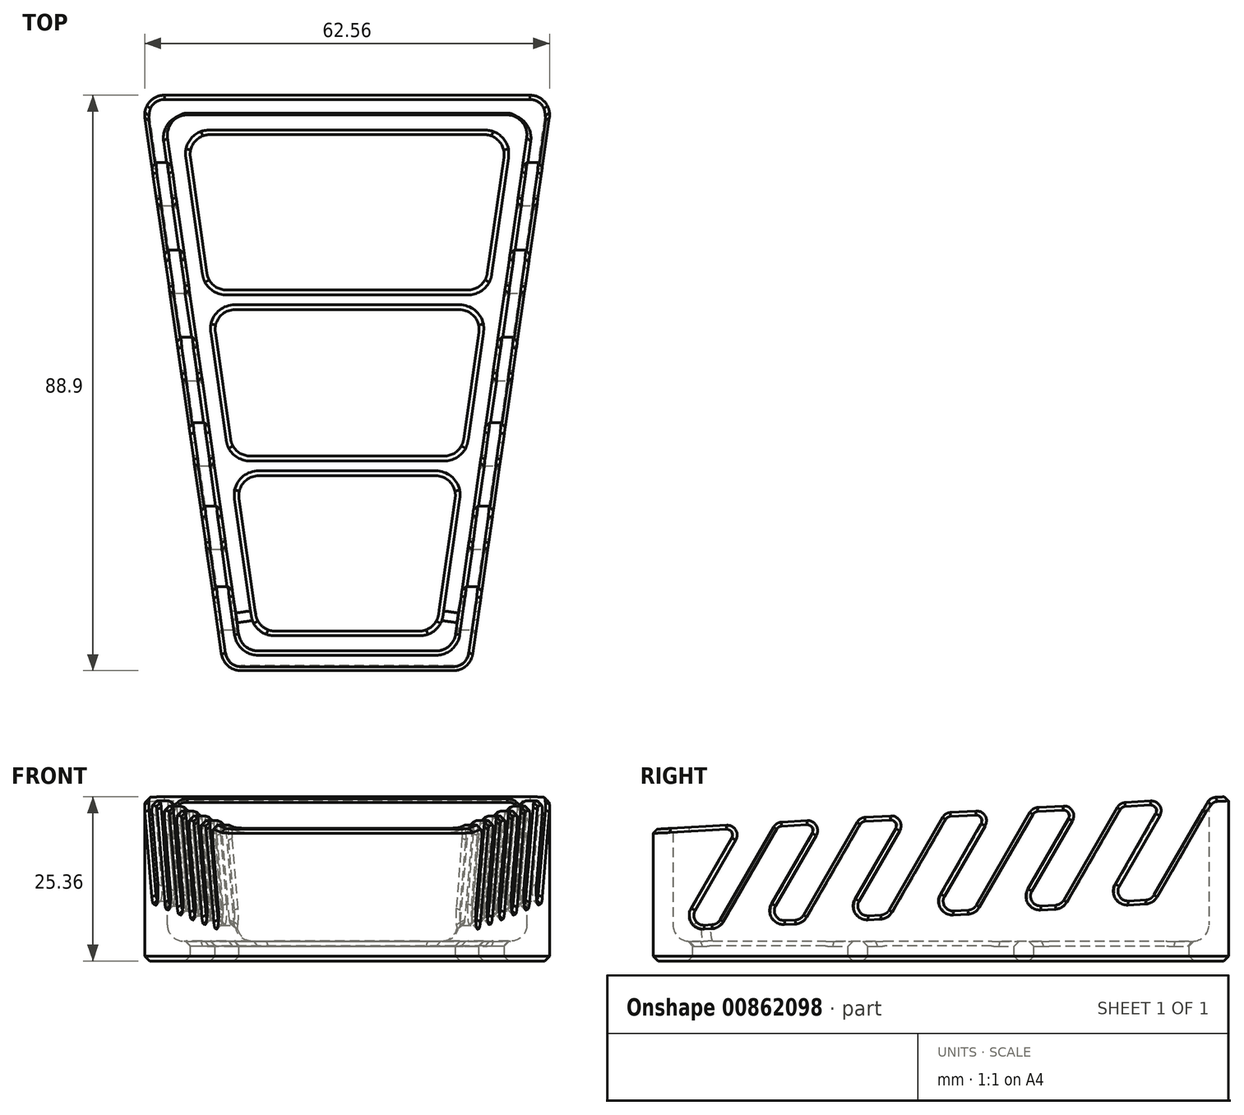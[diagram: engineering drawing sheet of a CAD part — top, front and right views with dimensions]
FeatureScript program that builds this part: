
annotation { "Feature Type Name" : "Feature", "Feature Type Description" : "" }
export const myFeature = defineFeature(function(context is Context, id is Id, definition is map)
    precondition{}
    {
        {
            var Q0;
            Q0=qCreatedBy(makeId("Top.planeOp"),FACE);
            var sketch = newSketch(context, id + "F0", { "sketchPlane" : qUnion([Q0])});
            skLineSegment(sketch, "E0", {"start": v(-122.84, 0) * mm, "end": v(0, 0) * mm, "construction": true});
            skLineSegment(sketch, "E1", {"start": v(0, 0) * mm, "end": v(0, 214.45) * mm, "construction": true});
            skLineSegment(sketch, "E2", {"start": v(-19.05, 0) * mm, "end": v(-31.75, 88.9) * mm});
            skLineSegment(sketch, "E3", {"start": v(-31.75, 88.9) * mm, "end": v(31.75, 88.9) * mm});
            skLineSegment(sketch, "E4", {"start": v(31.75, 88.9) * mm, "end": v(19.05, 0) * mm});
            skLineSegment(sketch, "E5", {"start": v(19.05, 0) * mm, "end": v(-19.05, 0) * mm});
            skSolve(sketch);
        }
        {
            var Q0;
            Q0 = qSketchRegion(id + "F0", true);
            extrude(context, id + "F1", {"entities" : qUnion([Q0]), "depth" : 25.4 * mm, "offsetDistance" : 25.4 * mm});
        }
        {
            var Q0;
            Q0=makeQuery(id+"F1.opExtrude","CAP_FACE",FACE,{"disambiguationData":[OSD([sQuery(id+"F0.wireOp",EDGE,"E2"),sQuery(id+"F0.wireOp",EDGE,"E3"),sQuery(id+"F0.wireOp",EDGE,"E4"),sQuery(id+"F0.wireOp",EDGE,"E5")])],"isStart":false});
            shell(context, id + "F2", {"entities" : qUnion([Q0]), "thickness" : 3.05 * mm});
        }
        {
            var Q0;
            Q0=qCreatedBy(makeId("Right.planeOp"),FACE);
            var sketch = newSketch(context, id + "F3", { "sketchPlane" : qUnion([Q0])});
            skLineSegment(sketch, "E6", {"start": v(88.9, 38.83) * mm, "end": v(88.9, 0) * mm, "construction": true});
            skLineSegment(sketch, "E7", {"start": v(0, 38.83) * mm, "end": v(0, 0) * mm, "construction": true});
            skLineSegment(sketch, "E8", {"start": v(0, 5.08) * mm, "end": v(88.9, 10.16) * mm, "construction": true});
            skLineSegment(sketch, "E9", {"start": v(101.6, 38.83) * mm, "end": v(-12.7, 38.83) * mm});
            skLineSegment(sketch, "E10", {"start": v(-12.7, 38.83) * mm, "end": v(-12.7, 19.6) * mm});
            skLineSegment(sketch, "E11", {"start": v(101.6, 38.83) * mm, "end": v(101.6, 26.13) * mm});
            skLineSegment(sketch, "E12", {"start": v(-12.7, 19.6) * mm, "end": v(14.18, 21.13) * mm});
            skLineSegment(sketch, "E13", {"start": v(16.6, 21.27) * mm, "end": v(7.5, 5.5) * mm, "construction": true});
            skLineSegment(sketch, "E14", {"start": v(29.27, 22) * mm, "end": v(20.17, 6.23) * mm, "construction": true});
            skLineSegment(sketch, "E15", {"start": v(42.31, 22.74) * mm, "end": v(33.21, 6.98) * mm, "construction": true});
            skLineSegment(sketch, "E16", {"start": v(55.66, 23.5) * mm, "end": v(46.56, 7.74) * mm, "construction": true});
            skLineSegment(sketch, "E17", {"start": v(69.15, 24.27) * mm, "end": v(60.05, 8.51) * mm, "construction": true});
            skLineSegment(sketch, "E18", {"start": v(82.88, 25.06) * mm, "end": v(73.78, 9.3) * mm, "construction": true});
            skLineSegment(sketch, "E19", {"start": v(14.18, 21.13) * mm, "end": v(5.08, 5.37) * mm});
            skLineSegment(sketch, "E20", {"start": v(5.08, 5.37) * mm, "end": v(9.93, 5.65) * mm});
            skLineSegment(sketch, "E21", {"start": v(9.93, 5.65) * mm, "end": v(19.03, 21.4) * mm});
            skLineSegment(sketch, "E22", {"start": v(26.61, 21.84) * mm, "end": v(17.52, 6.08) * mm});
            skLineSegment(sketch, "E23", {"start": v(17.52, 6.08) * mm, "end": v(22.82, 6.38) * mm});
            skLineSegment(sketch, "E24", {"start": v(22.82, 6.38) * mm, "end": v(31.92, 22.14) * mm});
            skLineSegment(sketch, "E25", {"start": v(39.5, 22.58) * mm, "end": v(30.4, 6.82) * mm});
            skLineSegment(sketch, "E26", {"start": v(30.4, 6.82) * mm, "end": v(36.02, 7.14) * mm});
            skLineSegment(sketch, "E27", {"start": v(36.02, 7.14) * mm, "end": v(45.12, 22.9) * mm});
            skLineSegment(sketch, "E28", {"start": v(52.7, 23.33) * mm, "end": v(43.6, 7.57) * mm});
            skLineSegment(sketch, "E29", {"start": v(43.6, 7.57) * mm, "end": v(49.51, 7.9) * mm});
            skLineSegment(sketch, "E30", {"start": v(49.51, 7.9) * mm, "end": v(58.61, 23.67) * mm});
            skLineSegment(sketch, "E31", {"start": v(66.2, 24.1) * mm, "end": v(57.1, 8.34) * mm});
            skLineSegment(sketch, "E32", {"start": v(57.1, 8.34) * mm, "end": v(63.01, 8.68) * mm});
            skLineSegment(sketch, "E33", {"start": v(63.01, 8.68) * mm, "end": v(72.1, 24.44) * mm});
            skLineSegment(sketch, "E34", {"start": v(79.7, 24.87) * mm, "end": v(70.6, 9.11) * mm});
            skLineSegment(sketch, "E35", {"start": v(70.6, 9.11) * mm, "end": v(76.96, 9.48) * mm});
            skLineSegment(sketch, "E36", {"start": v(76.96, 9.48) * mm, "end": v(86.06, 25.24) * mm});
            skPoint(sketch, "E37", {"position": v(0, 20.32) * mm});
            skPoint(sketch, "E38", {"position": v(88.9, 25.4) * mm});
            skLineSegment(sketch, "E39.trimOffspring", {"start": v(19.03, 21.4) * mm, "end": v(26.61, 21.84) * mm});
            skLineSegment(sketch, "E40.trimOffspring", {"start": v(31.92, 22.14) * mm, "end": v(39.5, 22.58) * mm});
            skLineSegment(sketch, "E41.trimOffspring", {"start": v(45.12, 22.9) * mm, "end": v(52.7, 23.33) * mm});
            skLineSegment(sketch, "E42.trimOffspring", {"start": v(58.61, 23.67) * mm, "end": v(66.2, 24.1) * mm});
            skLineSegment(sketch, "E43.trimOffspring", {"start": v(72.1, 24.44) * mm, "end": v(79.7, 24.87) * mm});
            skLineSegment(sketch, "E44.trimOffspring", {"start": v(86.06, 25.24) * mm, "end": v(101.6, 26.13) * mm});
            skSolve(sketch);
        }
        {
            var Q0;
            Q0=makeQuery(id+"F3.imprint","IMPRINT",FACE,{"disambiguationData":[TD([[makeQuery(id+"F3.imprint","IMPRINT",EDGE,{"derivedFrom":sQuery(id+"F3.wireOp",EDGE,"E9")}),1.0]])]});
            extrude(context, id + "F4", {"entities" : qUnion([Q0]), "operationType" : NewBodyOperationType.REMOVE, "endBound" : BoundingType.THROUGH_ALL, "depth" : 25.4 * mm, "offsetDistance" : 25.4 * mm, "hasSecondDirection" : true, "secondDirectionBound" : SecondDirectionBoundingType.THROUGH_ALL, "secondDirectionOppositeDirection" : true, "secondDirectionDepth" : 25.4 * mm});
        }
        {
            var Q0;
            Q0=makeQuery(id+"F2.opShell","OFFSET_FACE",FACE,{"disambiguationData":[OSD([sQuery(id+"F0.wireOp",EDGE,"E2"),sQuery(id+"F0.wireOp",EDGE,"E3"),sQuery(id+"F0.wireOp",EDGE,"E4"),sQuery(id+"F0.wireOp",EDGE,"E5")])]});
            var sketch = newSketch(context, id + "F5", { "sketchPlane" : qUnion([Q0])});
            skLineSegment(sketch, "E45", {"start": v(-38.97, 0) * mm, "end": v(0, 0) * mm, "construction": true});
            skLineSegment(sketch, "E46", {"start": v(0, 0) * mm, "end": v(0, 92.83) * mm, "construction": true});
            skLineSegment(sketch, "E47", {"start": v(-13.76, 6.1) * mm, "end": v(13.76, 6.1) * mm});
            skLineSegment(sketch, "E48", {"start": v(13.76, 6.1) * mm, "end": v(17.2, 30.1) * mm});
            skLineSegment(sketch, "E49", {"start": v(24.72, 82.8) * mm, "end": v(-24.72, 82.8) * mm});
            skLineSegment(sketch, "E50", {"start": v(-24.72, 82.8) * mm, "end": v(-21.3, 58.8) * mm});
            skLineSegment(sketch, "E51", {"start": v(-36.35, 31.62) * mm, "end": v(27.15, 31.62) * mm, "construction": true});
            skLineSegment(sketch, "E52", {"start": v(-39.3, 57.28) * mm, "end": v(34.58, 57.28) * mm, "construction": true});
            skLineSegment(sketch, "E53", {"start": v(-17.2, 30.1) * mm, "end": v(17.2, 30.1) * mm});
            skLineSegment(sketch, "E54", {"start": v(-17.63, 33.15) * mm, "end": v(17.63, 33.15) * mm});
            skLineSegment(sketch, "E55", {"start": v(-20.86, 55.75) * mm, "end": v(20.86, 55.75) * mm});
            skLineSegment(sketch, "E56", {"start": v(-21.3, 58.8) * mm, "end": v(21.3, 58.8) * mm});
            skLineSegment(sketch, "E57.trimOffspring", {"start": v(-17.2, 30.1) * mm, "end": v(-13.76, 6.1) * mm});
            skLineSegment(sketch, "E58.trimOffspring", {"start": v(-20.86, 55.75) * mm, "end": v(-17.63, 33.15) * mm});
            skLineSegment(sketch, "E59.trimOffspring", {"start": v(21.3, 58.8) * mm, "end": v(24.72, 82.8) * mm});
            skLineSegment(sketch, "E60.trimOffspring", {"start": v(17.63, 33.15) * mm, "end": v(20.86, 55.75) * mm});
            skSolve(sketch);
        }
        {
            var Q0;
            Q0=makeQuery(id+"F5.imprint","IMPRINT",FACE,{"disambiguationData":[TD([[makeQuery(id+"F5.imprint","IMPRINT",EDGE,{"derivedFrom":sQuery(id+"F5.wireOp",EDGE,"E47")}),1.0]])]});
            var Q1;
            Q1=makeQuery(id+"F5.imprint","IMPRINT",FACE,{"disambiguationData":[TD([[makeQuery(id+"F5.imprint","IMPRINT",EDGE,{"derivedFrom":sQuery(id+"F5.wireOp",EDGE,"E54")}),1.0]])]});
            var Q2;
            Q2=makeQuery(id+"F5.imprint","IMPRINT",FACE,{"disambiguationData":[TD([[makeQuery(id+"F5.imprint","IMPRINT",EDGE,{"derivedFrom":sQuery(id+"F5.wireOp",EDGE,"E49")}),1.0]])]});
            extrude(context, id + "F6", {"entities" : qUnion([Q0, Q1, Q2]), "operationType" : NewBodyOperationType.REMOVE, "oppositeDirection" : true, "depth" : 25.4 * mm, "offsetDistance" : 25.4 * mm});
        }
        {
            var Q0;
            Q0=makeQuery(id+"F6.boolean.opBoolean","COPY",EDGE,{"derivedFrom":makeQuery(id+"F6.opExtrude","SWEPT_EDGE",EDGE,{"disambiguationData":[OSD([sQuery(id+"F5.wireOp",EDGE,"E53"),sQuery(id+"F5.wireOp",EDGE,"E57.trimOffspring")])]})});
            var Q1;
            Q1=makeQuery(id+"F6.boolean.opBoolean","COPY",EDGE,{"derivedFrom":makeQuery(id+"F6.opExtrude","SWEPT_EDGE",EDGE,{"disambiguationData":[OSD([sQuery(id+"F5.wireOp",EDGE,"E54"),sQuery(id+"F5.wireOp",EDGE,"E58.trimOffspring")])]})});
            var Q2;
            Q2=makeQuery(id+"F6.boolean.opBoolean","COPY",EDGE,{"derivedFrom":makeQuery(id+"F6.opExtrude","SWEPT_EDGE",EDGE,{"disambiguationData":[OSD([sQuery(id+"F5.wireOp",EDGE,"E55"),sQuery(id+"F5.wireOp",EDGE,"E58.trimOffspring")])]})});
            var Q3;
            Q3=makeQuery(id+"F6.boolean.opBoolean","COPY",EDGE,{"derivedFrom":makeQuery(id+"F6.opExtrude","SWEPT_EDGE",EDGE,{"disambiguationData":[OSD([sQuery(id+"F5.wireOp",EDGE,"E50"),sQuery(id+"F5.wireOp",EDGE,"E56")])]})});
            var Q4;
            Q4=makeQuery(id+"F6.boolean.opBoolean","COPY",EDGE,{"derivedFrom":makeQuery(id+"F6.opExtrude","SWEPT_EDGE",EDGE,{"disambiguationData":[OSD([sQuery(id+"F5.wireOp",EDGE,"E47"),sQuery(id+"F5.wireOp",EDGE,"E57.trimOffspring")])]})});
            var Q5;
            Q5=makeQuery(id+"F6.boolean.opBoolean","COPY",EDGE,{"derivedFrom":makeQuery(id+"F6.opExtrude","SWEPT_EDGE",EDGE,{"disambiguationData":[OSD([sQuery(id+"F5.wireOp",EDGE,"E49"),sQuery(id+"F5.wireOp",EDGE,"E50")])]})});
            var Q6;
            Q6=makeQuery(id+"F6.boolean.opBoolean","COPY",EDGE,{"derivedFrom":makeQuery(id+"F6.opExtrude","SWEPT_EDGE",EDGE,{"disambiguationData":[OSD([sQuery(id+"F5.wireOp",EDGE,"E49"),sQuery(id+"F5.wireOp",EDGE,"E59.trimOffspring")])]})});
            var Q7;
            Q7=makeQuery(id+"F6.boolean.opBoolean","COPY",EDGE,{"derivedFrom":makeQuery(id+"F6.opExtrude","SWEPT_EDGE",EDGE,{"disambiguationData":[OSD([sQuery(id+"F5.wireOp",EDGE,"E55"),sQuery(id+"F5.wireOp",EDGE,"E60.trimOffspring")])]})});
            var Q8;
            Q8=makeQuery(id+"F6.boolean.opBoolean","COPY",EDGE,{"derivedFrom":makeQuery(id+"F6.opExtrude","SWEPT_EDGE",EDGE,{"disambiguationData":[OSD([sQuery(id+"F5.wireOp",EDGE,"E48"),sQuery(id+"F5.wireOp",EDGE,"E53")])]})});
            var Q9;
            Q9=makeQuery(id+"F6.boolean.opBoolean","COPY",EDGE,{"derivedFrom":makeQuery(id+"F6.opExtrude","SWEPT_EDGE",EDGE,{"disambiguationData":[OSD([sQuery(id+"F5.wireOp",EDGE,"E47"),sQuery(id+"F5.wireOp",EDGE,"E48")])]})});
            var Q10;
            Q10=makeQuery(id+"F6.boolean.opBoolean","COPY",EDGE,{"derivedFrom":makeQuery(id+"F6.opExtrude","SWEPT_EDGE",EDGE,{"disambiguationData":[OSD([sQuery(id+"F5.wireOp",EDGE,"E54"),sQuery(id+"F5.wireOp",EDGE,"E60.trimOffspring")])]})});
            var Q11;
            Q11=makeQuery(id+"F6.boolean.opBoolean","COPY",EDGE,{"derivedFrom":makeQuery(id+"F6.opExtrude","SWEPT_EDGE",EDGE,{"disambiguationData":[OSD([sQuery(id+"F5.wireOp",EDGE,"E56"),sQuery(id+"F5.wireOp",EDGE,"E59.trimOffspring")])]})});
            fillet(context, id + "F7", {"entities" : qUnion([Q0, Q1, Q2, Q3, Q4, Q5, Q6, Q7, Q8, Q9, Q10, Q11]), "radius" : 3.05 * mm, "tangentPropagation" : true, "allowEdgeOverflow" : false});
        }
        {
            var Q0;
            {var subQ0=sQuery(id+"F0.wireOp",EDGE,"E4");var subQ1=sQuery(id+"F3.wireOp",EDGE,"E19");var subQ2=sQuery(id+"F3.wireOp",EDGE,"E20");Q0=makeQuery(id+"F4.boolean.opBoolean","COPY",EDGE,{"disambiguationData":[TD([makeQuery(id+"F1.opExtrude","SWEPT_FACE",FACE,{"disambiguationData":[OSD([subQ0])]})])],"derivedFrom":makeQuery(id+"F4.opExtrude","SWEPT_EDGE",EDGE,{"disambiguationData":[OSD([subQ1,subQ2])]})});}
            var Q1;
            {var subQ0=sQuery(id+"F0.wireOp",EDGE,"E4");var subQ1=sQuery(id+"F3.wireOp",EDGE,"E20");var subQ2=sQuery(id+"F3.wireOp",EDGE,"E21");Q1=makeQuery(id+"F4.boolean.opBoolean","COPY",EDGE,{"disambiguationData":[TD([makeQuery(id+"F1.opExtrude","SWEPT_FACE",FACE,{"disambiguationData":[OSD([subQ0])]})])],"derivedFrom":makeQuery(id+"F4.opExtrude","SWEPT_EDGE",EDGE,{"disambiguationData":[OSD([subQ1,subQ2])]})});}
            var Q2;
            {var subQ0=sQuery(id+"F0.wireOp",EDGE,"E4");var subQ1=sQuery(id+"F3.wireOp",EDGE,"E12");var subQ2=sQuery(id+"F3.wireOp",EDGE,"E19");Q2=makeQuery(id+"F4.boolean.opBoolean","COPY",EDGE,{"disambiguationData":[TD([makeQuery(id+"F1.opExtrude","SWEPT_FACE",FACE,{"disambiguationData":[OSD([subQ0])]})])],"derivedFrom":makeQuery(id+"F4.opExtrude","SWEPT_EDGE",EDGE,{"disambiguationData":[OSD([subQ1,subQ2])]})});}
            var Q3;
            {var subQ0=sQuery(id+"F0.wireOp",EDGE,"E4");var subQ1=sQuery(id+"F3.wireOp",EDGE,"E21");var subQ2=sQuery(id+"F3.wireOp",EDGE,"E39.trimOffspring");Q3=makeQuery(id+"F4.boolean.opBoolean","COPY",EDGE,{"disambiguationData":[TD([makeQuery(id+"F1.opExtrude","SWEPT_FACE",FACE,{"disambiguationData":[OSD([subQ0])]})])],"derivedFrom":makeQuery(id+"F4.opExtrude","SWEPT_EDGE",EDGE,{"disambiguationData":[OSD([subQ1,subQ2])]})});}
            var Q4;
            {var subQ0=sQuery(id+"F0.wireOp",EDGE,"E4");var subQ1=sQuery(id+"F3.wireOp",EDGE,"E22");var subQ2=sQuery(id+"F3.wireOp",EDGE,"E39.trimOffspring");Q4=makeQuery(id+"F4.boolean.opBoolean","COPY",EDGE,{"disambiguationData":[TD([makeQuery(id+"F1.opExtrude","SWEPT_FACE",FACE,{"disambiguationData":[OSD([subQ0])]})])],"derivedFrom":makeQuery(id+"F4.opExtrude","SWEPT_EDGE",EDGE,{"disambiguationData":[OSD([subQ1,subQ2])]})});}
            var Q5;
            {var subQ0=sQuery(id+"F0.wireOp",EDGE,"E4");var subQ1=sQuery(id+"F3.wireOp",EDGE,"E40.trimOffspring");var subQ2=sQuery(id+"F3.wireOp",EDGE,"E24");Q5=makeQuery(id+"F4.boolean.opBoolean","COPY",EDGE,{"disambiguationData":[TD([makeQuery(id+"F1.opExtrude","SWEPT_FACE",FACE,{"disambiguationData":[OSD([subQ0])]})])],"derivedFrom":makeQuery(id+"F4.opExtrude","SWEPT_EDGE",EDGE,{"disambiguationData":[OSD([subQ2,subQ1])]})});}
            var Q6;
            {var subQ0=sQuery(id+"F0.wireOp",EDGE,"E4");var subQ1=sQuery(id+"F3.wireOp",EDGE,"E23");var subQ2=sQuery(id+"F3.wireOp",EDGE,"E22");Q6=makeQuery(id+"F4.boolean.opBoolean","COPY",EDGE,{"disambiguationData":[TD([makeQuery(id+"F1.opExtrude","SWEPT_FACE",FACE,{"disambiguationData":[OSD([subQ0])]})])],"derivedFrom":makeQuery(id+"F4.opExtrude","SWEPT_EDGE",EDGE,{"disambiguationData":[OSD([subQ2,subQ1])]})});}
            var Q7;
            {var subQ0=sQuery(id+"F0.wireOp",EDGE,"E4");var subQ1=sQuery(id+"F3.wireOp",EDGE,"E23");var subQ2=sQuery(id+"F3.wireOp",EDGE,"E24");Q7=makeQuery(id+"F4.boolean.opBoolean","COPY",EDGE,{"disambiguationData":[TD([makeQuery(id+"F1.opExtrude","SWEPT_FACE",FACE,{"disambiguationData":[OSD([subQ0])]})])],"derivedFrom":makeQuery(id+"F4.opExtrude","SWEPT_EDGE",EDGE,{"disambiguationData":[OSD([subQ1,subQ2])]})});}
            var Q8;
            {var subQ0=sQuery(id+"F0.wireOp",EDGE,"E4");var subQ1=sQuery(id+"F3.wireOp",EDGE,"E40.trimOffspring");var subQ2=sQuery(id+"F3.wireOp",EDGE,"E25");Q8=makeQuery(id+"F4.boolean.opBoolean","COPY",EDGE,{"disambiguationData":[TD([makeQuery(id+"F1.opExtrude","SWEPT_FACE",FACE,{"disambiguationData":[OSD([subQ0])]})])],"derivedFrom":makeQuery(id+"F4.opExtrude","SWEPT_EDGE",EDGE,{"disambiguationData":[OSD([subQ2,subQ1])]})});}
            var Q9;
            {var subQ0=sQuery(id+"F0.wireOp",EDGE,"E4");var subQ1=sQuery(id+"F3.wireOp",EDGE,"E27");var subQ2=sQuery(id+"F3.wireOp",EDGE,"E41.trimOffspring");Q9=makeQuery(id+"F4.boolean.opBoolean","COPY",EDGE,{"disambiguationData":[TD([makeQuery(id+"F1.opExtrude","SWEPT_FACE",FACE,{"disambiguationData":[OSD([subQ0])]})])],"derivedFrom":makeQuery(id+"F4.opExtrude","SWEPT_EDGE",EDGE,{"disambiguationData":[OSD([subQ1,subQ2])]})});}
            var Q10;
            {var subQ0=sQuery(id+"F0.wireOp",EDGE,"E4");var subQ1=sQuery(id+"F3.wireOp",EDGE,"E26");var subQ2=sQuery(id+"F3.wireOp",EDGE,"E27");Q10=makeQuery(id+"F4.boolean.opBoolean","COPY",EDGE,{"disambiguationData":[TD([makeQuery(id+"F1.opExtrude","SWEPT_FACE",FACE,{"disambiguationData":[OSD([subQ0])]})])],"derivedFrom":makeQuery(id+"F4.opExtrude","SWEPT_EDGE",EDGE,{"disambiguationData":[OSD([subQ1,subQ2])]})});}
            var Q11;
            {var subQ0=sQuery(id+"F0.wireOp",EDGE,"E4");var subQ1=sQuery(id+"F3.wireOp",EDGE,"E25");var subQ2=sQuery(id+"F3.wireOp",EDGE,"E26");Q11=makeQuery(id+"F4.boolean.opBoolean","COPY",EDGE,{"disambiguationData":[TD([makeQuery(id+"F1.opExtrude","SWEPT_FACE",FACE,{"disambiguationData":[OSD([subQ0])]})])],"derivedFrom":makeQuery(id+"F4.opExtrude","SWEPT_EDGE",EDGE,{"disambiguationData":[OSD([subQ1,subQ2])]})});}
            var Q12;
            {var subQ0=sQuery(id+"F0.wireOp",EDGE,"E4");var subQ1=sQuery(id+"F3.wireOp",EDGE,"E28");var subQ2=sQuery(id+"F3.wireOp",EDGE,"E29");Q12=makeQuery(id+"F4.boolean.opBoolean","COPY",EDGE,{"disambiguationData":[TD([makeQuery(id+"F1.opExtrude","SWEPT_FACE",FACE,{"disambiguationData":[OSD([subQ0])]})])],"derivedFrom":makeQuery(id+"F4.opExtrude","SWEPT_EDGE",EDGE,{"disambiguationData":[OSD([subQ1,subQ2])]})});}
            var Q13;
            {var subQ0=sQuery(id+"F0.wireOp",EDGE,"E4");var subQ1=sQuery(id+"F3.wireOp",EDGE,"E28");var subQ2=sQuery(id+"F3.wireOp",EDGE,"E41.trimOffspring");Q13=makeQuery(id+"F4.boolean.opBoolean","COPY",EDGE,{"disambiguationData":[TD([makeQuery(id+"F1.opExtrude","SWEPT_FACE",FACE,{"disambiguationData":[OSD([subQ0])]})])],"derivedFrom":makeQuery(id+"F4.opExtrude","SWEPT_EDGE",EDGE,{"disambiguationData":[OSD([subQ1,subQ2])]})});}
            var Q14;
            {var subQ0=sQuery(id+"F0.wireOp",EDGE,"E4");var subQ1=sQuery(id+"F3.wireOp",EDGE,"E30");var subQ2=sQuery(id+"F3.wireOp",EDGE,"E42.trimOffspring");Q14=makeQuery(id+"F4.boolean.opBoolean","COPY",EDGE,{"disambiguationData":[TD([makeQuery(id+"F1.opExtrude","SWEPT_FACE",FACE,{"disambiguationData":[OSD([subQ0])]})])],"derivedFrom":makeQuery(id+"F4.opExtrude","SWEPT_EDGE",EDGE,{"disambiguationData":[OSD([subQ1,subQ2])]})});}
            var Q15;
            {var subQ0=sQuery(id+"F0.wireOp",EDGE,"E4");var subQ1=sQuery(id+"F3.wireOp",EDGE,"E29");var subQ2=sQuery(id+"F3.wireOp",EDGE,"E30");Q15=makeQuery(id+"F4.boolean.opBoolean","COPY",EDGE,{"disambiguationData":[TD([makeQuery(id+"F1.opExtrude","SWEPT_FACE",FACE,{"disambiguationData":[OSD([subQ0])]})])],"derivedFrom":makeQuery(id+"F4.opExtrude","SWEPT_EDGE",EDGE,{"disambiguationData":[OSD([subQ1,subQ2])]})});}
            var Q16;
            {var subQ0=sQuery(id+"F0.wireOp",EDGE,"E4");var subQ1=sQuery(id+"F3.wireOp",EDGE,"E33");var subQ2=sQuery(id+"F3.wireOp",EDGE,"E43.trimOffspring");Q16=makeQuery(id+"F4.boolean.opBoolean","COPY",EDGE,{"disambiguationData":[TD([makeQuery(id+"F1.opExtrude","SWEPT_FACE",FACE,{"disambiguationData":[OSD([subQ0])]})])],"derivedFrom":makeQuery(id+"F4.opExtrude","SWEPT_EDGE",EDGE,{"disambiguationData":[OSD([subQ1,subQ2])]})});}
            var Q17;
            {var subQ0=sQuery(id+"F0.wireOp",EDGE,"E4");var subQ1=sQuery(id+"F3.wireOp",EDGE,"E31");var subQ2=sQuery(id+"F3.wireOp",EDGE,"E42.trimOffspring");Q17=makeQuery(id+"F4.boolean.opBoolean","COPY",EDGE,{"disambiguationData":[TD([makeQuery(id+"F1.opExtrude","SWEPT_FACE",FACE,{"disambiguationData":[OSD([subQ0])]})])],"derivedFrom":makeQuery(id+"F4.opExtrude","SWEPT_EDGE",EDGE,{"disambiguationData":[OSD([subQ1,subQ2])]})});}
            var Q18;
            {var subQ0=sQuery(id+"F0.wireOp",EDGE,"E4");var subQ1=sQuery(id+"F3.wireOp",EDGE,"E33");var subQ2=sQuery(id+"F3.wireOp",EDGE,"E32");Q18=makeQuery(id+"F4.boolean.opBoolean","COPY",EDGE,{"disambiguationData":[TD([makeQuery(id+"F1.opExtrude","SWEPT_FACE",FACE,{"disambiguationData":[OSD([subQ0])]})])],"derivedFrom":makeQuery(id+"F4.opExtrude","SWEPT_EDGE",EDGE,{"disambiguationData":[OSD([subQ2,subQ1])]})});}
            var Q19;
            {var subQ0=sQuery(id+"F0.wireOp",EDGE,"E4");var subQ1=sQuery(id+"F3.wireOp",EDGE,"E31");var subQ2=sQuery(id+"F3.wireOp",EDGE,"E32");Q19=makeQuery(id+"F4.boolean.opBoolean","COPY",EDGE,{"disambiguationData":[TD([makeQuery(id+"F1.opExtrude","SWEPT_FACE",FACE,{"disambiguationData":[OSD([subQ0])]})])],"derivedFrom":makeQuery(id+"F4.opExtrude","SWEPT_EDGE",EDGE,{"disambiguationData":[OSD([subQ1,subQ2])]})});}
            var Q20;
            {var subQ0=sQuery(id+"F0.wireOp",EDGE,"E4");var subQ1=sQuery(id+"F3.wireOp",EDGE,"E34");var subQ2=sQuery(id+"F3.wireOp",EDGE,"E43.trimOffspring");Q20=makeQuery(id+"F4.boolean.opBoolean","COPY",EDGE,{"disambiguationData":[TD([makeQuery(id+"F1.opExtrude","SWEPT_FACE",FACE,{"disambiguationData":[OSD([subQ0])]})])],"derivedFrom":makeQuery(id+"F4.opExtrude","SWEPT_EDGE",EDGE,{"disambiguationData":[OSD([subQ1,subQ2])]})});}
            var Q21;
            {var subQ0=sQuery(id+"F0.wireOp",EDGE,"E4");var subQ1=sQuery(id+"F3.wireOp",EDGE,"E35");var subQ2=sQuery(id+"F3.wireOp",EDGE,"E36");Q21=makeQuery(id+"F4.boolean.opBoolean","COPY",EDGE,{"disambiguationData":[TD([makeQuery(id+"F1.opExtrude","SWEPT_FACE",FACE,{"disambiguationData":[OSD([subQ0])]})])],"derivedFrom":makeQuery(id+"F4.opExtrude","SWEPT_EDGE",EDGE,{"disambiguationData":[OSD([subQ1,subQ2])]})});}
            var Q22;
            {var subQ0=sQuery(id+"F0.wireOp",EDGE,"E4");var subQ1=sQuery(id+"F3.wireOp",EDGE,"E34");var subQ2=sQuery(id+"F3.wireOp",EDGE,"E35");Q22=makeQuery(id+"F4.boolean.opBoolean","COPY",EDGE,{"disambiguationData":[TD([makeQuery(id+"F1.opExtrude","SWEPT_FACE",FACE,{"disambiguationData":[OSD([subQ0])]})])],"derivedFrom":makeQuery(id+"F4.opExtrude","SWEPT_EDGE",EDGE,{"disambiguationData":[OSD([subQ1,subQ2])]})});}
            var Q23;
            Q23=makeQuery(id+"F4.boolean.opBoolean","COPY",EDGE,{"derivedFrom":makeQuery(id+"F4.opExtrude","SWEPT_EDGE",EDGE,{"disambiguationData":[OSD([sQuery(id+"F3.wireOp",EDGE,"E36"),sQuery(id+"F3.wireOp",EDGE,"E44.trimOffspring")])]})});
            var Q24;
            {var subQ0=sQuery(id+"F0.wireOp",EDGE,"E2");var subQ1=sQuery(id+"F3.wireOp",EDGE,"E19");var subQ2=sQuery(id+"F3.wireOp",EDGE,"E12");Q24=makeQuery(id+"F4.boolean.opBoolean","COPY",EDGE,{"disambiguationData":[TD([makeQuery(id+"F1.opExtrude","SWEPT_FACE",FACE,{"disambiguationData":[OSD([subQ0])]})])],"derivedFrom":makeQuery(id+"F4.opExtrude","SWEPT_EDGE",EDGE,{"disambiguationData":[OSD([subQ2,subQ1])]})});}
            var Q25;
            {var subQ0=sQuery(id+"F0.wireOp",EDGE,"E2");var subQ1=sQuery(id+"F3.wireOp",EDGE,"E19");var subQ2=sQuery(id+"F3.wireOp",EDGE,"E20");Q25=makeQuery(id+"F4.boolean.opBoolean","COPY",EDGE,{"disambiguationData":[TD([makeQuery(id+"F1.opExtrude","SWEPT_FACE",FACE,{"disambiguationData":[OSD([subQ0])]})])],"derivedFrom":makeQuery(id+"F4.opExtrude","SWEPT_EDGE",EDGE,{"disambiguationData":[OSD([subQ1,subQ2])]})});}
            var Q26;
            {var subQ0=sQuery(id+"F0.wireOp",EDGE,"E2");var subQ1=sQuery(id+"F3.wireOp",EDGE,"E21");var subQ2=sQuery(id+"F3.wireOp",EDGE,"E39.trimOffspring");Q26=makeQuery(id+"F4.boolean.opBoolean","COPY",EDGE,{"disambiguationData":[TD([makeQuery(id+"F1.opExtrude","SWEPT_FACE",FACE,{"disambiguationData":[OSD([subQ0])]})])],"derivedFrom":makeQuery(id+"F4.opExtrude","SWEPT_EDGE",EDGE,{"disambiguationData":[OSD([subQ1,subQ2])]})});}
            var Q27;
            {var subQ0=sQuery(id+"F0.wireOp",EDGE,"E2");var subQ1=sQuery(id+"F3.wireOp",EDGE,"E22");var subQ2=sQuery(id+"F3.wireOp",EDGE,"E39.trimOffspring");Q27=makeQuery(id+"F4.boolean.opBoolean","COPY",EDGE,{"disambiguationData":[TD([makeQuery(id+"F1.opExtrude","SWEPT_FACE",FACE,{"disambiguationData":[OSD([subQ0])]})])],"derivedFrom":makeQuery(id+"F4.opExtrude","SWEPT_EDGE",EDGE,{"disambiguationData":[OSD([subQ1,subQ2])]})});}
            var Q28;
            {var subQ0=sQuery(id+"F0.wireOp",EDGE,"E2");var subQ1=sQuery(id+"F3.wireOp",EDGE,"E22");var subQ2=sQuery(id+"F3.wireOp",EDGE,"E23");Q28=makeQuery(id+"F4.boolean.opBoolean","COPY",EDGE,{"disambiguationData":[TD([makeQuery(id+"F1.opExtrude","SWEPT_FACE",FACE,{"disambiguationData":[OSD([subQ0])]})])],"derivedFrom":makeQuery(id+"F4.opExtrude","SWEPT_EDGE",EDGE,{"disambiguationData":[OSD([subQ1,subQ2])]})});}
            var Q29;
            {var subQ0=sQuery(id+"F0.wireOp",EDGE,"E2");var subQ1=sQuery(id+"F3.wireOp",EDGE,"E20");var subQ2=sQuery(id+"F3.wireOp",EDGE,"E21");Q29=makeQuery(id+"F4.boolean.opBoolean","COPY",EDGE,{"disambiguationData":[TD([makeQuery(id+"F1.opExtrude","SWEPT_FACE",FACE,{"disambiguationData":[OSD([subQ0])]})])],"derivedFrom":makeQuery(id+"F4.opExtrude","SWEPT_EDGE",EDGE,{"disambiguationData":[OSD([subQ1,subQ2])]})});}
            var Q30;
            {var subQ0=sQuery(id+"F0.wireOp",EDGE,"E2");var subQ1=sQuery(id+"F3.wireOp",EDGE,"E24");var subQ2=sQuery(id+"F3.wireOp",EDGE,"E23");Q30=makeQuery(id+"F4.boolean.opBoolean","COPY",EDGE,{"disambiguationData":[TD([makeQuery(id+"F1.opExtrude","SWEPT_FACE",FACE,{"disambiguationData":[OSD([subQ0])]})])],"derivedFrom":makeQuery(id+"F4.opExtrude","SWEPT_EDGE",EDGE,{"disambiguationData":[OSD([subQ2,subQ1])]})});}
            var Q31;
            {var subQ0=sQuery(id+"F0.wireOp",EDGE,"E2");var subQ1=sQuery(id+"F3.wireOp",EDGE,"E24");var subQ2=sQuery(id+"F3.wireOp",EDGE,"E40.trimOffspring");Q31=makeQuery(id+"F4.boolean.opBoolean","COPY",EDGE,{"disambiguationData":[TD([makeQuery(id+"F1.opExtrude","SWEPT_FACE",FACE,{"disambiguationData":[OSD([subQ0])]})])],"derivedFrom":makeQuery(id+"F4.opExtrude","SWEPT_EDGE",EDGE,{"disambiguationData":[OSD([subQ1,subQ2])]})});}
            var Q32;
            {var subQ0=sQuery(id+"F0.wireOp",EDGE,"E2");var subQ1=sQuery(id+"F3.wireOp",EDGE,"E41.trimOffspring");var subQ2=sQuery(id+"F3.wireOp",EDGE,"E27");Q32=makeQuery(id+"F4.boolean.opBoolean","COPY",EDGE,{"disambiguationData":[TD([makeQuery(id+"F1.opExtrude","SWEPT_FACE",FACE,{"disambiguationData":[OSD([subQ0])]})])],"derivedFrom":makeQuery(id+"F4.opExtrude","SWEPT_EDGE",EDGE,{"disambiguationData":[OSD([subQ2,subQ1])]})});}
            var Q33;
            {var subQ0=sQuery(id+"F0.wireOp",EDGE,"E2");var subQ1=sQuery(id+"F3.wireOp",EDGE,"E26");var subQ2=sQuery(id+"F3.wireOp",EDGE,"E27");Q33=makeQuery(id+"F4.boolean.opBoolean","COPY",EDGE,{"disambiguationData":[TD([makeQuery(id+"F1.opExtrude","SWEPT_FACE",FACE,{"disambiguationData":[OSD([subQ0])]})])],"derivedFrom":makeQuery(id+"F4.opExtrude","SWEPT_EDGE",EDGE,{"disambiguationData":[OSD([subQ1,subQ2])]})});}
            var Q34;
            {var subQ0=sQuery(id+"F0.wireOp",EDGE,"E2");var subQ1=sQuery(id+"F3.wireOp",EDGE,"E25");var subQ2=sQuery(id+"F3.wireOp",EDGE,"E40.trimOffspring");Q34=makeQuery(id+"F4.boolean.opBoolean","COPY",EDGE,{"disambiguationData":[TD([makeQuery(id+"F1.opExtrude","SWEPT_FACE",FACE,{"disambiguationData":[OSD([subQ0])]})])],"derivedFrom":makeQuery(id+"F4.opExtrude","SWEPT_EDGE",EDGE,{"disambiguationData":[OSD([subQ1,subQ2])]})});}
            var Q35;
            {var subQ0=sQuery(id+"F0.wireOp",EDGE,"E2");var subQ1=sQuery(id+"F3.wireOp",EDGE,"E25");var subQ2=sQuery(id+"F3.wireOp",EDGE,"E26");Q35=makeQuery(id+"F4.boolean.opBoolean","COPY",EDGE,{"disambiguationData":[TD([makeQuery(id+"F1.opExtrude","SWEPT_FACE",FACE,{"disambiguationData":[OSD([subQ0])]})])],"derivedFrom":makeQuery(id+"F4.opExtrude","SWEPT_EDGE",EDGE,{"disambiguationData":[OSD([subQ1,subQ2])]})});}
            var Q36;
            {var subQ0=sQuery(id+"F0.wireOp",EDGE,"E2");var subQ1=sQuery(id+"F3.wireOp",EDGE,"E29");var subQ2=sQuery(id+"F3.wireOp",EDGE,"E28");Q36=makeQuery(id+"F4.boolean.opBoolean","COPY",EDGE,{"disambiguationData":[TD([makeQuery(id+"F1.opExtrude","SWEPT_FACE",FACE,{"disambiguationData":[OSD([subQ0])]})])],"derivedFrom":makeQuery(id+"F4.opExtrude","SWEPT_EDGE",EDGE,{"disambiguationData":[OSD([subQ2,subQ1])]})});}
            var Q37;
            {var subQ0=sQuery(id+"F0.wireOp",EDGE,"E2");var subQ1=sQuery(id+"F3.wireOp",EDGE,"E41.trimOffspring");var subQ2=sQuery(id+"F3.wireOp",EDGE,"E28");Q37=makeQuery(id+"F4.boolean.opBoolean","COPY",EDGE,{"disambiguationData":[TD([makeQuery(id+"F1.opExtrude","SWEPT_FACE",FACE,{"disambiguationData":[OSD([subQ0])]})])],"derivedFrom":makeQuery(id+"F4.opExtrude","SWEPT_EDGE",EDGE,{"disambiguationData":[OSD([subQ2,subQ1])]})});}
            var Q38;
            {var subQ0=sQuery(id+"F0.wireOp",EDGE,"E2");var subQ1=sQuery(id+"F3.wireOp",EDGE,"E30");var subQ2=sQuery(id+"F3.wireOp",EDGE,"E42.trimOffspring");Q38=makeQuery(id+"F4.boolean.opBoolean","COPY",EDGE,{"disambiguationData":[TD([makeQuery(id+"F1.opExtrude","SWEPT_FACE",FACE,{"disambiguationData":[OSD([subQ0])]})])],"derivedFrom":makeQuery(id+"F4.opExtrude","SWEPT_EDGE",EDGE,{"disambiguationData":[OSD([subQ1,subQ2])]})});}
            var Q39;
            {var subQ0=sQuery(id+"F0.wireOp",EDGE,"E2");var subQ1=sQuery(id+"F3.wireOp",EDGE,"E31");var subQ2=sQuery(id+"F3.wireOp",EDGE,"E32");Q39=makeQuery(id+"F4.boolean.opBoolean","COPY",EDGE,{"disambiguationData":[TD([makeQuery(id+"F1.opExtrude","SWEPT_FACE",FACE,{"disambiguationData":[OSD([subQ0])]})])],"derivedFrom":makeQuery(id+"F4.opExtrude","SWEPT_EDGE",EDGE,{"disambiguationData":[OSD([subQ1,subQ2])]})});}
            var Q40;
            {var subQ0=sQuery(id+"F0.wireOp",EDGE,"E2");var subQ1=sQuery(id+"F3.wireOp",EDGE,"E33");var subQ2=sQuery(id+"F3.wireOp",EDGE,"E43.trimOffspring");Q40=makeQuery(id+"F4.boolean.opBoolean","COPY",EDGE,{"disambiguationData":[TD([makeQuery(id+"F1.opExtrude","SWEPT_FACE",FACE,{"disambiguationData":[OSD([subQ0])]})])],"derivedFrom":makeQuery(id+"F4.opExtrude","SWEPT_EDGE",EDGE,{"disambiguationData":[OSD([subQ1,subQ2])]})});}
            var Q41;
            {var subQ0=sQuery(id+"F0.wireOp",EDGE,"E2");var subQ1=sQuery(id+"F3.wireOp",EDGE,"E42.trimOffspring");var subQ2=sQuery(id+"F3.wireOp",EDGE,"E31");Q41=makeQuery(id+"F4.boolean.opBoolean","COPY",EDGE,{"disambiguationData":[TD([makeQuery(id+"F1.opExtrude","SWEPT_FACE",FACE,{"disambiguationData":[OSD([subQ0])]})])],"derivedFrom":makeQuery(id+"F4.opExtrude","SWEPT_EDGE",EDGE,{"disambiguationData":[OSD([subQ2,subQ1])]})});}
            var Q42;
            {var subQ0=sQuery(id+"F0.wireOp",EDGE,"E2");var subQ1=sQuery(id+"F3.wireOp",EDGE,"E29");var subQ2=sQuery(id+"F3.wireOp",EDGE,"E30");Q42=makeQuery(id+"F4.boolean.opBoolean","COPY",EDGE,{"disambiguationData":[TD([makeQuery(id+"F1.opExtrude","SWEPT_FACE",FACE,{"disambiguationData":[OSD([subQ0])]})])],"derivedFrom":makeQuery(id+"F4.opExtrude","SWEPT_EDGE",EDGE,{"disambiguationData":[OSD([subQ1,subQ2])]})});}
            var Q43;
            {var subQ0=sQuery(id+"F0.wireOp",EDGE,"E2");var subQ1=sQuery(id+"F3.wireOp",EDGE,"E32");var subQ2=sQuery(id+"F3.wireOp",EDGE,"E33");Q43=makeQuery(id+"F4.boolean.opBoolean","COPY",EDGE,{"disambiguationData":[TD([makeQuery(id+"F1.opExtrude","SWEPT_FACE",FACE,{"disambiguationData":[OSD([subQ0])]})])],"derivedFrom":makeQuery(id+"F4.opExtrude","SWEPT_EDGE",EDGE,{"disambiguationData":[OSD([subQ1,subQ2])]})});}
            var Q44;
            {var subQ0=sQuery(id+"F0.wireOp",EDGE,"E2");var subQ1=sQuery(id+"F3.wireOp",EDGE,"E35");var subQ2=sQuery(id+"F3.wireOp",EDGE,"E36");Q44=makeQuery(id+"F4.boolean.opBoolean","COPY",EDGE,{"disambiguationData":[TD([makeQuery(id+"F1.opExtrude","SWEPT_FACE",FACE,{"disambiguationData":[OSD([subQ0])]})])],"derivedFrom":makeQuery(id+"F4.opExtrude","SWEPT_EDGE",EDGE,{"disambiguationData":[OSD([subQ1,subQ2])]})});}
            var Q45;
            {var subQ0=sQuery(id+"F0.wireOp",EDGE,"E2");var subQ1=sQuery(id+"F3.wireOp",EDGE,"E34");var subQ2=sQuery(id+"F3.wireOp",EDGE,"E35");Q45=makeQuery(id+"F4.boolean.opBoolean","COPY",EDGE,{"disambiguationData":[TD([makeQuery(id+"F1.opExtrude","SWEPT_FACE",FACE,{"disambiguationData":[OSD([subQ0])]})])],"derivedFrom":makeQuery(id+"F4.opExtrude","SWEPT_EDGE",EDGE,{"disambiguationData":[OSD([subQ1,subQ2])]})});}
            var Q46;
            {var subQ0=sQuery(id+"F0.wireOp",EDGE,"E2");var subQ1=sQuery(id+"F3.wireOp",EDGE,"E34");var subQ2=sQuery(id+"F3.wireOp",EDGE,"E43.trimOffspring");Q46=makeQuery(id+"F4.boolean.opBoolean","COPY",EDGE,{"disambiguationData":[TD([makeQuery(id+"F1.opExtrude","SWEPT_FACE",FACE,{"disambiguationData":[OSD([subQ0])]})])],"derivedFrom":makeQuery(id+"F4.opExtrude","SWEPT_EDGE",EDGE,{"disambiguationData":[OSD([subQ1,subQ2])]})});}
            fillet(context, id + "F8", {"entities" : qUnion([Q0, Q1, Q2, Q3, Q4, Q5, Q6, Q7, Q8, Q9, Q10, Q11, Q12, Q13, Q14, Q15, Q16, Q17, Q18, Q19, Q20, Q21, Q22, Q23, Q24, Q25, Q26, Q27, Q28, Q29, Q30, Q31, Q32, Q33, Q34, Q35, Q36, Q37, Q38, Q39, Q40, Q41, Q42, Q43, Q44, Q45, Q46]), "radius" : 1.52 * mm, "tangentPropagation" : true, "allowEdgeOverflow" : false});
        }
        {
            var Q0;
            Q0=makeQuery(id+"F2.opShell","OFFSET_EDGE",EDGE,{"disambiguationData":[OSD([sQuery(id+"F0.wireOp",EDGE,"E3"),sQuery(id+"F0.wireOp",EDGE,"E4")])]});
            var Q1;
            Q1=makeQuery(id+"F2.opShell","OFFSET_EDGE",EDGE,{"disambiguationData":[OSD([sQuery(id+"F0.wireOp",EDGE,"E2"),sQuery(id+"F0.wireOp",EDGE,"E3")])]});
            var Q2;
            Q2=makeQuery(id+"F2.opShell","OFFSET_EDGE",EDGE,{"disambiguationData":[OSD([sQuery(id+"F0.wireOp",EDGE,"E2"),sQuery(id+"F0.wireOp",EDGE,"E5")])]});
            var Q3;
            Q3=makeQuery(id+"F2.opShell","OFFSET_EDGE",EDGE,{"disambiguationData":[OSD([sQuery(id+"F0.wireOp",EDGE,"E4"),sQuery(id+"F0.wireOp",EDGE,"E5")])]});
            var Q4;
            Q4=makeQuery(id+"F1.opExtrude","SWEPT_EDGE",EDGE,{"disambiguationData":[OSD([sQuery(id+"F0.wireOp",EDGE,"E4"),sQuery(id+"F0.wireOp",EDGE,"E5")])]});
            var Q5;
            Q5=makeQuery(id+"F1.opExtrude","SWEPT_EDGE",EDGE,{"disambiguationData":[OSD([sQuery(id+"F0.wireOp",EDGE,"E3"),sQuery(id+"F0.wireOp",EDGE,"E4")])]});
            var Q6;
            Q6=makeQuery(id+"F1.opExtrude","SWEPT_EDGE",EDGE,{"disambiguationData":[OSD([sQuery(id+"F0.wireOp",EDGE,"E2"),sQuery(id+"F0.wireOp",EDGE,"E3")])]});
            var Q7;
            Q7=makeQuery(id+"F1.opExtrude","SWEPT_EDGE",EDGE,{"disambiguationData":[OSD([sQuery(id+"F0.wireOp",EDGE,"E2"),sQuery(id+"F0.wireOp",EDGE,"E5")])]});
            fillet(context, id + "F9", {"entities" : qUnion([Q0, Q1, Q2, Q3, Q4, Q5, Q6, Q7]), "radius" : 3.05 * mm, "tangentPropagation" : true, "allowEdgeOverflow" : false});
        }
        {
            var Q0;
            {var subQ0=sQuery(id+"F0.wireOp",EDGE,"E4");Q0=makeQuery(id+"F2.opShell","OFFSET_EDGE",EDGE,{"disambiguationData":[OSD([subQ0]),TDD([makeQuery(id+"F1.opExtrude","CAP_EDGE",EDGE,{"disambiguationData":[OSD([subQ0])],"isStart":true})])]});}
            fillet(context, id + "F10", {"entities" : qUnion([Q0]), "radius" : 2.54 * mm, "tangentPropagation" : true, "allowEdgeOverflow" : false});
        }
        {
            var Q0;
            Q0=makeQuery(id+"F1.opExtrude","CAP_FACE",FACE,{"disambiguationData":[OSD([sQuery(id+"F0.wireOp",EDGE,"E2"),sQuery(id+"F0.wireOp",EDGE,"E3"),sQuery(id+"F0.wireOp",EDGE,"E4"),sQuery(id+"F0.wireOp",EDGE,"E5")])],"isStart":true});
            var Q1;
            Q1=makeQuery(id+"F7.opFillet","BLEND_EDGE",EDGE,{"blendedFrom":[makeQuery(id+"F6.boolean.opBoolean","COPY",EDGE,{"derivedFrom":makeQuery(id+"F6.opExtrude","SWEPT_EDGE",EDGE,{"disambiguationData":[OSD([sQuery(id+"F5.wireOp",EDGE,"E53"),sQuery(id+"F5.wireOp",EDGE,"E57.trimOffspring")])]})}),makeQuery(id+"F2.opShell","OFFSET_FACE",FACE,{"disambiguationData":[OSD([sQuery(id+"F0.wireOp",EDGE,"E2"),sQuery(id+"F0.wireOp",EDGE,"E3"),sQuery(id+"F0.wireOp",EDGE,"E4"),sQuery(id+"F0.wireOp",EDGE,"E5")])]})],"blendedInto":[makeQuery(id+"F2.opShell","OFFSET_FACE",FACE,{"disambiguationData":[OSD([sQuery(id+"F0.wireOp",EDGE,"E2"),sQuery(id+"F0.wireOp",EDGE,"E3"),sQuery(id+"F0.wireOp",EDGE,"E4"),sQuery(id+"F0.wireOp",EDGE,"E5")])]})]});
            var Q2;
            Q2=makeQuery(id+"F7.opFillet","BLEND_EDGE",EDGE,{"blendedFrom":[makeQuery(id+"F6.boolean.opBoolean","COPY",EDGE,{"derivedFrom":makeQuery(id+"F6.opExtrude","SWEPT_EDGE",EDGE,{"disambiguationData":[OSD([sQuery(id+"F5.wireOp",EDGE,"E54"),sQuery(id+"F5.wireOp",EDGE,"E58.trimOffspring")])]})}),makeQuery(id+"F2.opShell","OFFSET_FACE",FACE,{"disambiguationData":[OSD([sQuery(id+"F0.wireOp",EDGE,"E2"),sQuery(id+"F0.wireOp",EDGE,"E3"),sQuery(id+"F0.wireOp",EDGE,"E4"),sQuery(id+"F0.wireOp",EDGE,"E5")])]})],"blendedInto":[makeQuery(id+"F2.opShell","OFFSET_FACE",FACE,{"disambiguationData":[OSD([sQuery(id+"F0.wireOp",EDGE,"E2"),sQuery(id+"F0.wireOp",EDGE,"E3"),sQuery(id+"F0.wireOp",EDGE,"E4"),sQuery(id+"F0.wireOp",EDGE,"E5")])]})]});
            var Q3;
            Q3=makeQuery(id+"F7.opFillet","BLEND_EDGE",EDGE,{"blendedFrom":[makeQuery(id+"F6.boolean.opBoolean","COPY",EDGE,{"derivedFrom":makeQuery(id+"F6.opExtrude","SWEPT_EDGE",EDGE,{"disambiguationData":[OSD([sQuery(id+"F5.wireOp",EDGE,"E50"),sQuery(id+"F5.wireOp",EDGE,"E56")])]})}),makeQuery(id+"F2.opShell","OFFSET_FACE",FACE,{"disambiguationData":[OSD([sQuery(id+"F0.wireOp",EDGE,"E2"),sQuery(id+"F0.wireOp",EDGE,"E3"),sQuery(id+"F0.wireOp",EDGE,"E4"),sQuery(id+"F0.wireOp",EDGE,"E5")])]})],"blendedInto":[makeQuery(id+"F2.opShell","OFFSET_FACE",FACE,{"disambiguationData":[OSD([sQuery(id+"F0.wireOp",EDGE,"E2"),sQuery(id+"F0.wireOp",EDGE,"E3"),sQuery(id+"F0.wireOp",EDGE,"E4"),sQuery(id+"F0.wireOp",EDGE,"E5")])]})]});
            chamfer(context, id + "F11", {"entities" : qUnion([Q0, Q1, Q2, Q3]), "width" : 0.76 * mm, "tangentPropagation" : true});
        }
        {
            var Q0;
            Q0=makeQuery(id+"F4.boolean.opBoolean","INTERSECT",EDGE,{"derivedFrom":[makeQuery(id+"F1.opExtrude","SWEPT_FACE",FACE,{"disambiguationData":[OSD([sQuery(id+"F0.wireOp",EDGE,"E4")])]}),makeQuery(id+"F4.opExtrude","SWEPT_FACE",FACE,{"disambiguationData":[OSD([sQuery(id+"F3.wireOp",EDGE,"E41.trimOffspring")])]})]});
            var Q1;
            Q1=makeQuery(id+"F4.boolean.opBoolean","INTERSECT",EDGE,{"derivedFrom":[makeQuery(id+"F2.opShell","OFFSET_FACE",FACE,{"disambiguationData":[OSD([sQuery(id+"F0.wireOp",EDGE,"E4")])]}),makeQuery(id+"F4.opExtrude","SWEPT_FACE",FACE,{"disambiguationData":[OSD([sQuery(id+"F3.wireOp",EDGE,"E42.trimOffspring")])]})]});
            chamfer(context, id + "F12", {"entities" : qUnion([Q0, Q1]), "width" : 0.64 * mm, "tangentPropagation" : true});
        }
    });
